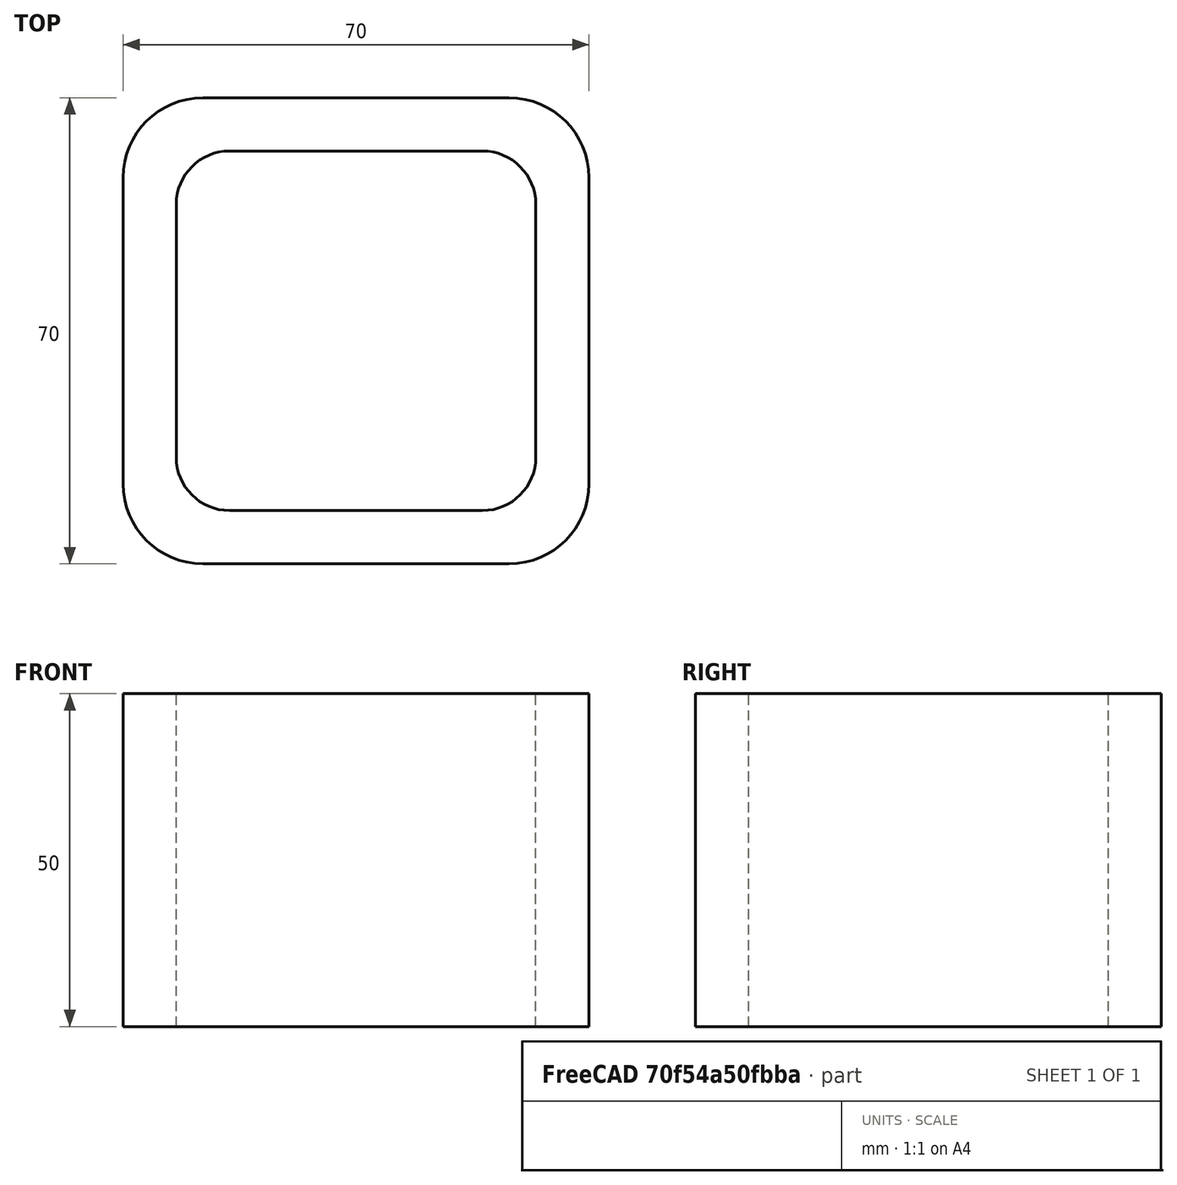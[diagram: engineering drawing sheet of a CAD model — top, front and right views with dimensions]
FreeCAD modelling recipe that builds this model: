
FCSTD DOCUMENT  (FreeCAD 0.15R4671 (Git))
Label: Square hollow section 70x70x8 EN10219 S235JRH
License: All rights reserved
LicenseURL: http://en.wikipedia.org/wiki/All_rights_reserved
objects: Sketcher::SketchObject×1, Part::Extrusion×1
note: 2 computed .brp shape members not serialized (recipe doc carries the construction recipe); baked Part::Feature solids carry a one-line shape summary decoded from their .brp

FEATURE [Sketcher::SketchObject] Sketch
  sketch-geometry (16):
    g0: LineSegment StartX=-19 StartY=27 StartZ=0 EndX=19 EndY=27 EndZ=0
    g1: LineSegment StartX=27 StartY=19 StartZ=0 EndX=27 EndY=-19 EndZ=0
    g2: LineSegment StartX=19 StartY=-27 StartZ=0 EndX=-19 EndY=-27 EndZ=0
    g3: LineSegment StartX=-27 StartY=-19 StartZ=0 EndX=-27 EndY=19 EndZ=0
    g4: LineSegment StartX=-23 StartY=35 StartZ=0 EndX=23 EndY=35 EndZ=0
    g5: LineSegment StartX=35 StartY=23 StartZ=0 EndX=35 EndY=-23 EndZ=0
    g6: LineSegment StartX=23 StartY=-35 StartZ=0 EndX=-23 EndY=-35 EndZ=0
    g7: LineSegment StartX=-35 StartY=-23 StartZ=0 EndX=-35 EndY=23 EndZ=0
    g8: ArcOfCircle CenterX=-19 CenterY=19 CenterZ=0 NormalX=0 NormalY=0 NormalZ=1 Radius=8 StartAngle=1.5708 EndAngle=3.14159
    g9: ArcOfCircle CenterX=19 CenterY=19 CenterZ=0 NormalX=0 NormalY=0 NormalZ=1 Radius=8 StartAngle=0 EndAngle=1.5708
    g10: ArcOfCircle CenterX=19 CenterY=-19 CenterZ=0 NormalX=0 NormalY=0 NormalZ=1 Radius=8 StartAngle=4.71239 EndAngle=6.28319
    g11: ArcOfCircle CenterX=-19 CenterY=-19 CenterZ=0 NormalX=0 NormalY=0 NormalZ=1 Radius=8 StartAngle=3.14159 EndAngle=4.71239
    g12: ArcOfCircle CenterX=23 CenterY=23 CenterZ=0 NormalX=0 NormalY=0 NormalZ=1 Radius=12 StartAngle=0 EndAngle=1.5708
    g13: ArcOfCircle CenterX=23 CenterY=-23 CenterZ=0 NormalX=0 NormalY=0 NormalZ=1 Radius=12 StartAngle=4.71239 EndAngle=6.28319
    g14: ArcOfCircle CenterX=-23 CenterY=-23 CenterZ=0 NormalX=0 NormalY=0 NormalZ=1 Radius=12 StartAngle=3.14159 EndAngle=4.71239
    g15: ArcOfCircle CenterX=-23 CenterY=23 CenterZ=0 NormalX=0 NormalY=0 NormalZ=1 Radius=12 StartAngle=1.5708 EndAngle=3.14159
  constraints (36):
    c: Horizontal(g2)
    c: Vertical(g3)
    c: Horizontal(g6)
    c: Vertical(g7)
    c: Tangent(g3,g8) = 1.5708
    c: Tangent(g0,g8) = 1.5708
    c: Tangent(g0,g9) = 1.5708
    c: Tangent(g1,g9) = 1.5708
    c: Tangent(g1,g10) = 1.5708
    c: Tangent(g2,g10) = 1.5708
    c: Tangent(g2,g11) = 1.5708
    c: Tangent(g3,g11) = 1.5708
    c: Tangent(g4,g12) = 1.5708
    c: Tangent(g5,g12) = 1.5708
    c: Tangent(g5,g13) = 1.5708
    c: Tangent(g6,g13) = 1.5708
    c: Tangent(g6,g14) = 1.5708
    c: Tangent(g7,g14) = 1.5708
    c: Tangent(g7,g15) = 1.5708
    c: Tangent(g4,g15) = 1.5708
    c: Equal(g9,g8)
    c: Equal(g9,g11)
    c: Equal(g9,g10)
    c: Equal(g12,g15)
    c: Equal(g12,g14)
    c: Equal(g12,g13)
    c: Symmetric(g4,g6,g-1)
    c: Symmetric(g7,g5,g-2)
    c: DistanceY(g4,g6) = -70
    c: DistanceX(g7,g5) = 70
    c: Symmetric(g3,g1,g-2)
    c: Symmetric(g0,g2,g-1)
    c: DistanceY(g0,g4) = 8
    c: DistanceX(g5,g1) = -8
    c: Radius(g9) = 8
    c: Radius(g12) = 12
FEATURE [Part::Extrusion] Extrude  label="Square hollow section 70x70x8 EN10219 S235JRH"
  Base = -> Sketch
  Dir = (0,0,50)
  Solid = true
